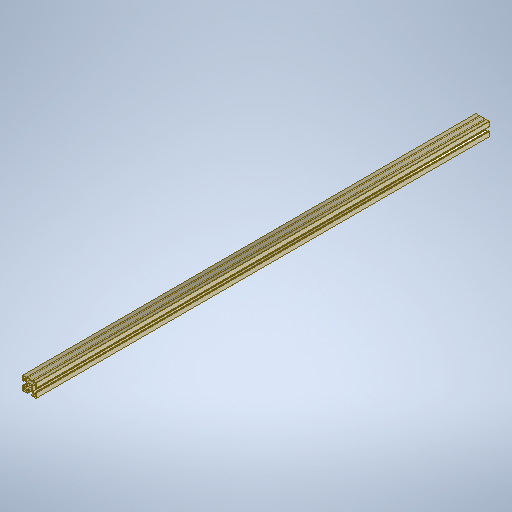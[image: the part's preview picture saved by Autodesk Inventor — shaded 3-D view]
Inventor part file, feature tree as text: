
AUTODESK INVENTOR PART (.ipt)
format: ipt  version: 2025.2 (Build 292293000, 293)  size: 456,192 bytes
history: native  units: mm
features: mirror x4, extrude x2, other x1, sketch x1
ambient origin geometry x8: Origin, YZ Plane, XZ Plane, XY Plane, X Axis, Y Axis, Z Axis, Center Point
bodies: Body1 (feature_tree)
feature tree (8):
  other  "Sólido4"
  sketch  "Esboço1"  dims[d0=10.0mm d1=15.0mm d2=30.0mm d3=8.0mm d5=8.2mm d7=1.1mm d10=4.5mm d13=1.1mm d14=11.5mm d16=1.1mm d21=2.2mm d25=2.2mm d26=1.1mm d35=1000.0mm d36=0.0mm d37=1000.0mm d38=0.0mm d29=0.5mm d30=0.872665mm d31=0.5mm d32=0.872665mm d33=0.5mm d34=0.872665mm]
  extrude  "Extrusão5"  Depth=15.0mm
  mirror  "Espelhar11"
  mirror  "Espelhar12"
  mirror  "Espelhar13"
  extrude  "Extrusão6"  Depth=30.0mm
  mirror  "Espelhar14"
